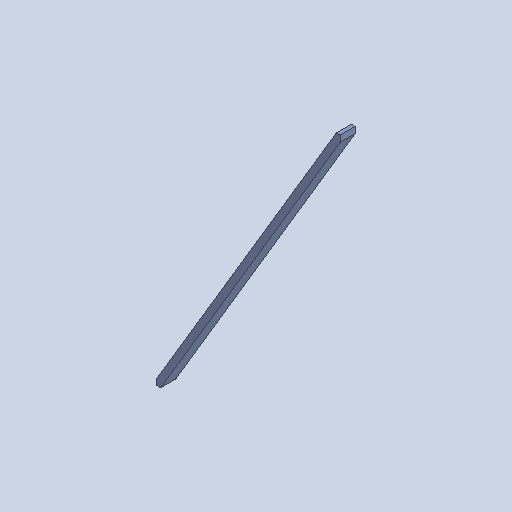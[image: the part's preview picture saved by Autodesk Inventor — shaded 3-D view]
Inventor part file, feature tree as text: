
AUTODESK INVENTOR PART (.ipt)
format: ipt  version: 2025.1 (Build 291241020, 241B)  size: 259,584 bytes
history: native  units: in
note: dims shown in document units (in); Inventor stores cm internally (conversion verified against a paired STEP export)
features: plane x1, extrude x1, sketch x1, other x1
ambient origin geometry x8: Origin, YZ Plane, XZ Plane, XY Plane, X Axis, Y Axis, Z Axis, Center Point
bodies: Solid1 (feature_tree)
feature tree (4):
  plane  "Work Plane1"
  extrude  "Extrusion1"  [1 undecoded]
  sketch  "Sketch1"  dims[d0=3.5in d1=0.0in]
  other  "Finish1"
note: 1 required parameter value undecoded (feature->parameter linkage not recoverable at this tier; creation-order binding heuristic only, values carry confidence <= 0.55)
